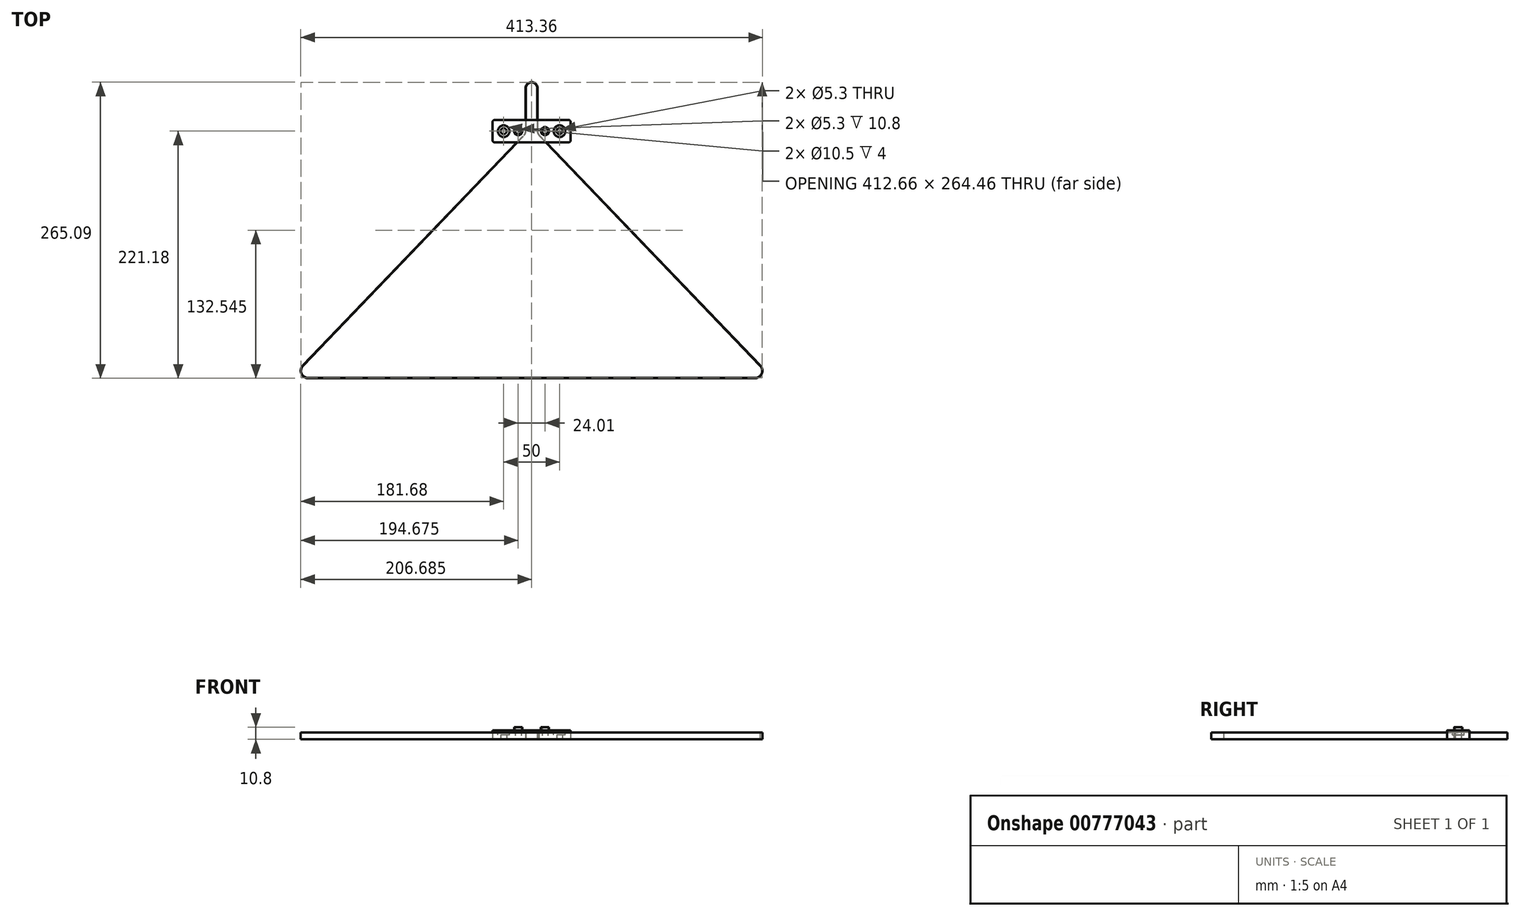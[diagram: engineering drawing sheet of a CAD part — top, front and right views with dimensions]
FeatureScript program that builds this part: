
annotation { "Feature Type Name" : "Feature", "Feature Type Description" : "" }
export const myFeature = defineFeature(function(context is Context, id is Id, definition is map)
    precondition{}
    {
        {
            var Q0;
            Q0=qCreatedBy(makeId("Top.planeOp"),FACE);
            var sketch = newSketch(context, id + "F0", { "sketchPlane" : qUnion([Q0])});
            skLineSegment(sketch, "E0", {"start": v(-200, 0) * mm, "end": v(200, 0) * mm, "construction": true});
            skLineSegment(sketch, "E1", {"start": v(200, 0) * mm, "end": v(0, 253) * mm, "construction": true});
            skLineSegment(sketch, "E2", {"start": v(0, 253) * mm, "end": v(-200, 0) * mm, "construction": true});
            skArc(sketch, "E3", {"start": v(-196.05, 5) * mm, "mid": v(-206.01, 2.09) * mm, "end": v(-200, -6.37) * mm});
            skArc(sketch, "E4", {"start": v(200, -6.37) * mm, "mid": v(205.88, -2.43) * mm, "end": v(204.5, 4.5) * mm});
            skLineSegment(sketch, "E5", {"start": v(-5.1, 254.78) * mm, "end": v(-5.12, 254.75) * mm});
            skLineSegment(sketch, "E6", {"start": v(5.1, 254.78) * mm, "end": v(5.12, 254.75) * mm});
            skLineSegment(sketch, "E7", {"start": v(200, -6.36) * mm, "end": v(-200, -6.37) * mm});
            skPoint(sketch, "E8.orphan", {"position": v(0, 261.18) * mm});
            skPoint(sketch, "E9.orphan", {"position": v(208.14, 0) * mm});
            skArc(sketch, "E10", {"start": v(-195.86, 5.24) * mm, "mid": v(-206.3, 2.2) * mm, "end": v(-200, -6.68) * mm});
            skArc(sketch, "E11", {"start": v(200, -6.68) * mm, "mid": v(206.14, -2.62) * mm, "end": v(204.82, 4.62) * mm});
            skLineSegment(sketch, "E12", {"start": v(-200, -6.68) * mm, "end": v(200, -6.68) * mm});
            skLineSegment(sketch, "E13.trimOffspring", {"start": v(0, 298.25) * mm, "end": v(0.15, 298.42) * mm});
            skPoint(sketch, "E14.orphan", {"position": v(243.86, 0) * mm});
            skArc(sketch, "E15", {"start": v(-6.83, 210.97) * mm, "mid": v(-5.78, 212.6) * mm, "end": v(-5.4, 214.5) * mm});
            skArc(sketch, "E16", {"start": v(5.41, 214.5) * mm, "mid": v(5.78, 212.6) * mm, "end": v(6.83, 210.97) * mm});
            skArc(sketch, "E17.converted", {"start": v(5.4, 253) * mm, "mid": v(0, 258.41) * mm, "end": v(-5.41, 253) * mm});
            skArc(sketch, "E18.converted", {"start": v(5.1, 253) * mm, "mid": v(0, 258.1) * mm, "end": v(-5.1, 253) * mm});
            skArc(sketch, "E19", {"start": v(-6.6, 210.75) * mm, "mid": v(-5.49, 212.48) * mm, "end": v(-5.1, 214.5) * mm});
            skArc(sketch, "E20", {"start": v(5.1, 214.5) * mm, "mid": v(5.5, 212.42) * mm, "end": v(6.69, 210.67) * mm});
            skLineSegment(sketch, "E21", {"start": v(-5.1, 254.82) * mm, "end": v(-5.1, 254.78) * mm});
            skLineSegment(sketch, "E22", {"start": v(5.1, 254.82) * mm, "end": v(5.1, 254.78) * mm});
            skLineSegment(sketch, "E23", {"start": v(5.4, 253) * mm, "end": v(5.41, 214.5) * mm});
            skLineSegment(sketch, "E24.trimOffspring", {"start": v(-5.41, 253) * mm, "end": v(-5.4, 214.5) * mm});
            skLineSegment(sketch, "E25.trimOffspring", {"start": v(-5.1, 253) * mm, "end": v(-5.1, 214.5) * mm});
            skLineSegment(sketch, "E26.trimOffspring", {"start": v(5.1, 253) * mm, "end": v(5.1, 214.5) * mm});
            skPoint(sketch, "E27.orphan", {"position": v(4.09, 256.55) * mm});
            skPoint(sketch, "E28.orphan", {"position": v(5.1, 256.55) * mm});
            skLineSegment(sketch, "E29", {"start": v(-204.82, 4.62) * mm, "end": v(-6.83, 210.97) * mm});
            skPoint(sketch, "E30.orphan", {"position": v(-209.26, 0) * mm});
            skLineSegment(sketch, "E31", {"start": v(-209.26, -0.45) * mm, "end": v(-6.6, 210.75) * mm});
            skLineSegment(sketch, "E32", {"start": v(6.83, 210.97) * mm, "end": v(204.82, 4.62) * mm});
            skLineSegment(sketch, "E33.trimOffspring", {"start": v(6.69, 210.67) * mm, "end": v(204.5, 4.5) * mm});
            skSolve(sketch);
        }
        {
            var Q0;
            Q0=qSketchRegion(id+"F0",true);
            extrude(context, id + "F1", {"entities" : qUnion([Q0]), "depth" : 6 * mm, "offsetDistance" : 25 * mm});
        }
        {
            var Q0;
            Q0=qCreatedBy(makeId("Top.planeOp"),FACE);
            var sketch = newSketch(context, id + "F2", { "sketchPlane" : qUnion([Q0])});
            skLineSegment(sketch, "E34.bottom", {"start": v(-35, 224.5) * mm, "end": v(35, 224.5) * mm});
            skLineSegment(sketch, "E34.top", {"start": v(-35, 204.5) * mm, "end": v(35, 204.5) * mm});
            skLineSegment(sketch, "E34.left", {"start": v(-35, 224.5) * mm, "end": v(-35, 204.5) * mm});
            skLineSegment(sketch, "E34.right", {"start": v(35, 224.5) * mm, "end": v(35, 204.5) * mm});
            skArc(sketch, "E35.0", {"start": v(-6.83, 210.97) * mm, "mid": v(-5.78, 212.6) * mm, "end": v(-5.4, 214.5) * mm, "construction": true});
            skArc(sketch, "E36.0", {"start": v(5.4, 214.5) * mm, "mid": v(5.78, 212.6) * mm, "end": v(6.83, 210.97) * mm, "construction": true});
            skCircle(sketch, "E37", {"center": v(12, 214.5) * mm, "radius": 2.65 * mm});
            skCircle(sketch, "E38", {"center": v(-12, 214.5) * mm, "radius": 2.65 * mm});
            skPoint(sketch, "E39", {"position": v(0, 283.12) * mm});
            skPoint(sketch, "E40", {"position": v(0, 224.5) * mm});
            skPoint(sketch, "E41", {"position": v(-35, 214.5) * mm});
            skCircle(sketch, "E42", {"center": v(-25, 214.5) * mm, "radius": 2.65 * mm});
            skCircle(sketch, "E43", {"center": v(25, 214.5) * mm, "radius": 2.65 * mm});
            skSolve(sketch);
        }
        {
            var Q0;
            Q0=qSketchRegion(id+"F2",true);
            extrude(context, id + "F3", {"entities" : qUnion([Q0]), "depth" : 8 * mm, "offsetDistance" : 25 * mm});
        }
        {
            var Q0;
            Q0=makeQuery(id+"F3.opExtrude","CAP_FACE",FACE,{"disambiguationData":[OSD([sQuery(id+"F2.wireOp",EDGE,"E34.bottom"),sQuery(id+"F2.wireOp",EDGE,"E34.top"),sQuery(id+"F2.wireOp",EDGE,"E34.left"),sQuery(id+"F2.wireOp",EDGE,"E34.right"),sQuery(id+"F2.wireOp",EDGE,"E37"),sQuery(id+"F2.wireOp",EDGE,"E38"),sQuery(id+"F2.wireOp",EDGE,"E42"),sQuery(id+"F2.wireOp",EDGE,"E43")])],"isStart":false});
            var sketch = newSketch(context, id + "F4", { "sketchPlane" : qUnion([Q0])});
            skPoint(sketch, "E44", {"position": v(-25, 214.5) * mm});
            skPoint(sketch, "E45", {"position": v(25, 214.5) * mm});
            skCircle(sketch, "E46", {"center": v(-25, 214.5) * mm, "radius": 5.25 * mm});
            skCircle(sketch, "E47", {"center": v(25, 214.5) * mm, "radius": 5.25 * mm});
            skSolve(sketch);
        }
        {
            var Q0;
            Q0=qSketchRegion(id+"F4",true);
            extrude(context, id + "F5", {"entities" : qUnion([Q0]), "operationType" : NewBodyOperationType.REMOVE, "oppositeDirection" : true, "depth" : 4 * mm, "offsetDistance" : 25 * mm});
        }
        {
            var Q0;
            Q0=makeQuery(id+"F3.opExtrude","CAP_FACE",FACE,{"disambiguationData":[OSD([sQuery(id+"F2.wireOp",EDGE,"E34.bottom"),sQuery(id+"F2.wireOp",EDGE,"E34.top"),sQuery(id+"F2.wireOp",EDGE,"E34.left"),sQuery(id+"F2.wireOp",EDGE,"E34.right"),sQuery(id+"F2.wireOp",EDGE,"E37"),sQuery(id+"F2.wireOp",EDGE,"E38"),sQuery(id+"F2.wireOp",EDGE,"E42"),sQuery(id+"F2.wireOp",EDGE,"E43")])],"isStart":false});
            var sketch = newSketch(context, id + "F6", { "sketchPlane" : qUnion([Q0])});
            skCircle(sketch, "E48.0", {"center": v(-12, 214.5) * mm, "radius": 2.65 * mm});
            skCircle(sketch, "E49.0", {"center": v(12, 214.5) * mm, "radius": 2.65 * mm});
            skCircle(sketch, "E50", {"center": v(-12, 214.5) * mm, "radius": 3.65 * mm});
            skCircle(sketch, "E51", {"center": v(12, 214.5) * mm, "radius": 3.65 * mm});
            skSolve(sketch);
        }
        {
            var Q0;
            Q0=qSketchRegion(id+"F6",true);
            extrude(context, id + "F7", {"entities" : qUnion([Q0]), "operationType" : NewBodyOperationType.ADD, "depth" : 2.8 * mm, "offsetDistance" : 25 * mm});
        }
        {
            var Q0;
            Q0=makeQuery(id+"F3.opExtrude","SWEPT_EDGE",EDGE,{"disambiguationData":[OSD([sQuery(id+"F2.wireOp",EDGE,"E34.top"),sQuery(id+"F2.wireOp",EDGE,"E34.left")])]});
            var Q1;
            Q1=makeQuery(id+"F3.opExtrude","SWEPT_EDGE",EDGE,{"disambiguationData":[OSD([sQuery(id+"F2.wireOp",EDGE,"E34.bottom"),sQuery(id+"F2.wireOp",EDGE,"E34.left")])]});
            var Q2;
            Q2=makeQuery(id+"F3.opExtrude","SWEPT_EDGE",EDGE,{"disambiguationData":[OSD([sQuery(id+"F2.wireOp",EDGE,"E34.bottom"),sQuery(id+"F2.wireOp",EDGE,"E34.right")])]});
            var Q3;
            Q3=makeQuery(id+"F3.opExtrude","SWEPT_EDGE",EDGE,{"disambiguationData":[OSD([sQuery(id+"F2.wireOp",EDGE,"E34.top"),sQuery(id+"F2.wireOp",EDGE,"E34.right")])]});
            fillet(context, id + "F8", {"entities" : qUnion([Q0, Q1, Q2, Q3]), "radius" : 2 * mm, "tangentPropagation" : true, "allowEdgeOverflow" : false});
        }
    });
